# Revit family: QF_ELECTROLUXPROFESSIONAL_1LSN97_WH6-33_E
name_source: partatom
category: Attrezzature speciali
units: mm (PartAtom-declared; Revit-internal decimal feet)

## family parameters
Basato su piano di lavoro = No
Condiviso = No
Punto di calcolo locali = No
Quota connettore circolare = Usa diametro
Sempre verticale = Sì
Taglio con vuoti quando caricato = No
Tipo di parte = Normale

## types (29) — shared parameters
Depth Actual = 1134 mm  [stored 3.72047 ft]
Height Actual = 1446 mm  [stored 4.74409 ft]
Latent Heat Output = 0.0
Length Actual = 1020 mm  [stored 3.34646 ft]
Modello = WH6-33
Produttore = Electrolux Professional
Sensible Heat Output = 0.0
URL = www.electroluxprofessional.com
Weight = 560
zero-valued in all types: Gas KW, Prospetto di default, Steam Pounds per Hour

## per-type parameters (varying)
| type | Cycle | Descrizione | Item Number | Phase | Volts | Watts |
| 9868130186 | 50 Hz | WASHER WH6-33 33KG EL 19,1KW 380-400/50/3N COMPASS PRO 6H12 SE 2xWATER POWDER+5xLIQ. VALV.OPEN SILVER 2.I/O QC DISCON. S | 1LA1A4 | 3 | 400 V | 19600 W |
| 9868130119 | 50 Hz | WASHER WH6-33 33KG EL 19,1KW 380-400/50/3N COMPASS PRO 6G01 ML 2xWATER POWDER+5xLIQ. VALV.OPEN SST/SILVER 2.I/O DISCON. | 1LSP3V | 3 | 400 V | 19600 W |
| 9868130181 | 50 Hz | WASHER WH6-33 33KG EL 19,8KW 415/50/3N COMPASS PRO 6G01 ML 2xWATER POWDER+5xLIQ. VALV.OPEN SST 2.I/O DISCON. STOP | 1L0GD5 | 3 | 415 V | 20100 W |
| 9868130355 | 60 Hz | WASHER WH6-33 33KG NO HEAT 208-240/60/1 COMPASS PRO 6G01 ML 2xWATER POWDER+5xLIQ. VALV.OPEN SILVER 2.I/O STOP | 1L0HE6 | 1 | 240 V | 3500 W |
| 9868130159 | 50 Hz | WASHER WH6-33 33KG EL 19,1KW 380-400/50/3N COMPASS PRO 6G01 ML 2xWATER POWDER+5xLIQ. VALV.OPEN SILVER 2.I/O DISCON. STOP | 1L822K | 3 | 400 V | 19600 W |
| 9868130171 | 50 Hz | WASHER WH6-33 33KG EL 19,1KW 380-400/220-230/50/3N/3 COMPASS PRO 6H12 ML 2xWATER POWDER+5xLIQ. VALV.OPEN SILVER 2.I/O QC | 1L0GBV | 3 | 400 V | 19600 W |
| 9868130370 | 50 Hz | WASHER WH6-33 33KG EL 9,5KW 380/220/50/3N/3 COMPASS PRO 6G01 ML 2xWATER POWDER+5xLIQ. EL.VALV.CLOSED SILVER 2.I/O QC DIS | 1L0HJD | 3 | 400 V | 9900 W |
| 9868130005 | 60 Hz | WH6-33 SG/SG/BL 19,8 EXUS 8S03 | 1L0EZF | 3 | 240 V | 20100 W |
| 9868130134 | 50 Hz | WASHER WH6-33 33KG NO HEAT 200/50/60/3 COMPASS PRO 6G41 JP,EN 2xWATER POWDER+5xLIQ. VALV.OPEN SST/SILVER 2.I/O DISCON. | 1LSP67 | 3 | 200 V | 3100 W |
| 9868130124 | 50 Hz | WASHER WH6-33 33KG EL 19,1KW 380-400/220-230/50/3N/3 COMPASS PRO 6G01 ML 2xWATER POWDER+5xLIQ. VALV.OPEN SST/SILVER 2.I/ | 1LSP63 | 3 | 400 V | 23300 W |
| 9868130263 | 50 Hz | WASHER WH6-33 33KG EL 14,4KW 200/50/60/3 COMPASS PRO 6H43 JP,EN 2xWATER POWDER+5xLIQ. VALV.OPEN SILVER 2.I/O DISCON. | 1LA24T | 3 | 200 V | 14800 W |
| 9868130174 | 50 Hz | WASHER WH6-33 33KG MOP 23KW 380-400/220-230/50/3N/3 COMPASS PRO 6M16 ML 2xWATER POWDER+5xLIQ. EL.VALV.CLOSED SILVER 2.I/ | 1L0GBY | 3 | 400 V | 23300 W |
| 9868130243 | 50 Hz | WASHER WH6-33 33KG EL 19,8KW 415/50/3N COMPASS PRO 6G01 ML 2xWATER POWDER+5xLIQ. EL.VALV.OPEN SILVER 2.I/O QC DISCON. ST | 1LSPE9 | 3 | 415 V | 20100 W |
| 9868130322 | 50 Hz | WASHER WH6-33 33KG EL 19,1KW 380-400/50/3N COMPASS PRO 6H12 SE 2xWATER 5xLIQ. VALV.OPEN SILVER 2.I/O DISCON. STOP | 1L0H31 | 3 | 400 V | 19600 W |
| 9868130006 | 60 Hz | WH6-33 SG/SG/BL 19,8 EXUS 8S03 | 1L0EZG | 3 | 240 V | 20100 W |
| 9868130182 | 50 Hz | WASHER WH6-33 33KG MOP 23KW 380-400/220-230/50/3N/3 COMPASS PRO 6M14 ML 2xWATER POWDER+5xLIQ. EL.VALV.OPEN SST/SILVER 2. | 1L0GD6 | 3 | 400 V | 23300 W |
| 9868130167 | 50 Hz | WASHER WH6-33 33KG MOP 23KW 380-400/220-230/50/3N/3 COMPASS PRO 6M17 ML 2xWATER POWDER+5xLIQ. EL.VALV.CLOSED SILVER 2.I/ | 1L0GAM | 3 | 400 V | 23300 W |
| 9868130172 | 50 Hz | WASHER WH6-33 33KG MOP 23KW 380-400/220-230/50/3N/3 COMPASS PRO 6M14 ML 2xWATER POWDER+5xLIQ. EL.VALV.OPEN SILVER 2.I/O | 1L0GBW | 3 | 400 V | 23300 W |
| 9868130162 | 50 Hz | WASHER WH6-33 33KG NO HEAT 200/50/60/3 COMPASS PRO 6G41 JP,EN 2xWATER POWDER+5xLIQ. VALV.OPEN SILVER 2.I/O DISCON. | 1L822N | 3 | 200 V | 3100 W |
| 9868130081 | 50 Hz | WASHER WH6-33 33KG EL 19,8KW 415/50/3N COMPASS PRO 6G01 ML 2xWATER POWDER+5xLIQ. VALV.OPEN SST/SILVER 2.I/O DISCON. STOP | 1LA1D8 | 3 | 415 V | 20100 W |
| 9868130252 | 50 Hz | WASHER WH6-33 33KG NO HEAT 220-240/50/1N COMPASS PRO 6G01 ML 2xWATER POWDER+5xLIQ. VALV.OPEN SILVER 2.I/O QC DISCON. STO | 1L0GRW | 1 | 240 V | 3500 W |
| 9868130242 | 60 Hz | WASHER WH6-33 33KG EL 21KW 440/60/3 COMPASS PRO 6G07 ML 2xWATER POWDER+5xLIQ. VALV.OPEN SILVER 2.I/O QC TRAFO DISCON. ST | 1L999Z | 3 | 440 V | 21400 W |
| 9868130160 | 50 Hz | WASHER WH6-33 33KG EL 19,1KW 380-400/220-230/50/3N/3 COMPASS PRO 6G01 ML 2xWATER POWDER+5xLIQ. VALV.OPEN SILVER 2.I/O DI | 1L822L | 3 | 400 V | 19600 W |
| 9868130227 | 50 Hz | WASHER WH6-33 33KG EL 19,8KW 415/50/3N COMPASS PRO 6H12 ML 2xWATER POWDER+5xLIQ. EL.VALV.CLOSED SST 2.I/O DISCON. STOP | 1LSPDU | 3 | 415 V | 20100 W |
| 9868130183 | 50 Hz | WASHER WH6-33 33KG MOP 23KW 380-400/220-230/50/3N/3 COMPASS PRO 6M14 ML 2xWATER POWDER+5xLIQ. EL.VALV.OPEN SILVER 2.I/O | 1LA1A1 | 3 | 400 V | 23300 W |
| 9868130088 | 50 Hz | WASHER WH6-33 33KG EL 19,8KW 415/50/3N COMPASS PRO 6G01 ML 2xWATER POWDER+5xLIQ. VALV.OPEN SILVER 2.I/O DISCON. STOP | 1L8253 | 3 | 415 V | 20100 W |
| 9868130234 | 60 Hz | WASHER WH6-33 33KG NO HEAT 220-240/60/1N COMPASS PRO 6G01 ML 2xWATER POWDER+5xLIQ. VALV.OPEN SILVER 2.I/O QC DISCON. STO | 1LA22J | 1 | 240 V | 3500 W |
| 9868130007 | 60 Hz | WH6-33 SG/SG/BL 19,8 EXUS 8S03 | 1L0EZH | 3 | 240 V | 20100 W |
| 9868130008 | 60 Hz | WH6-33 SG/SG/BL 19,8 EXUS 8S03 | 1L0EZJ | 3 | 240 V | 20100 W |

note: [stored X ft] marks values corroborated as IEEE doubles in the binary element streams (Revit-internal decimal feet)

## geometry (parser evidence)
native form markers: Blend x8
no freeform markers — native parametric forms only
